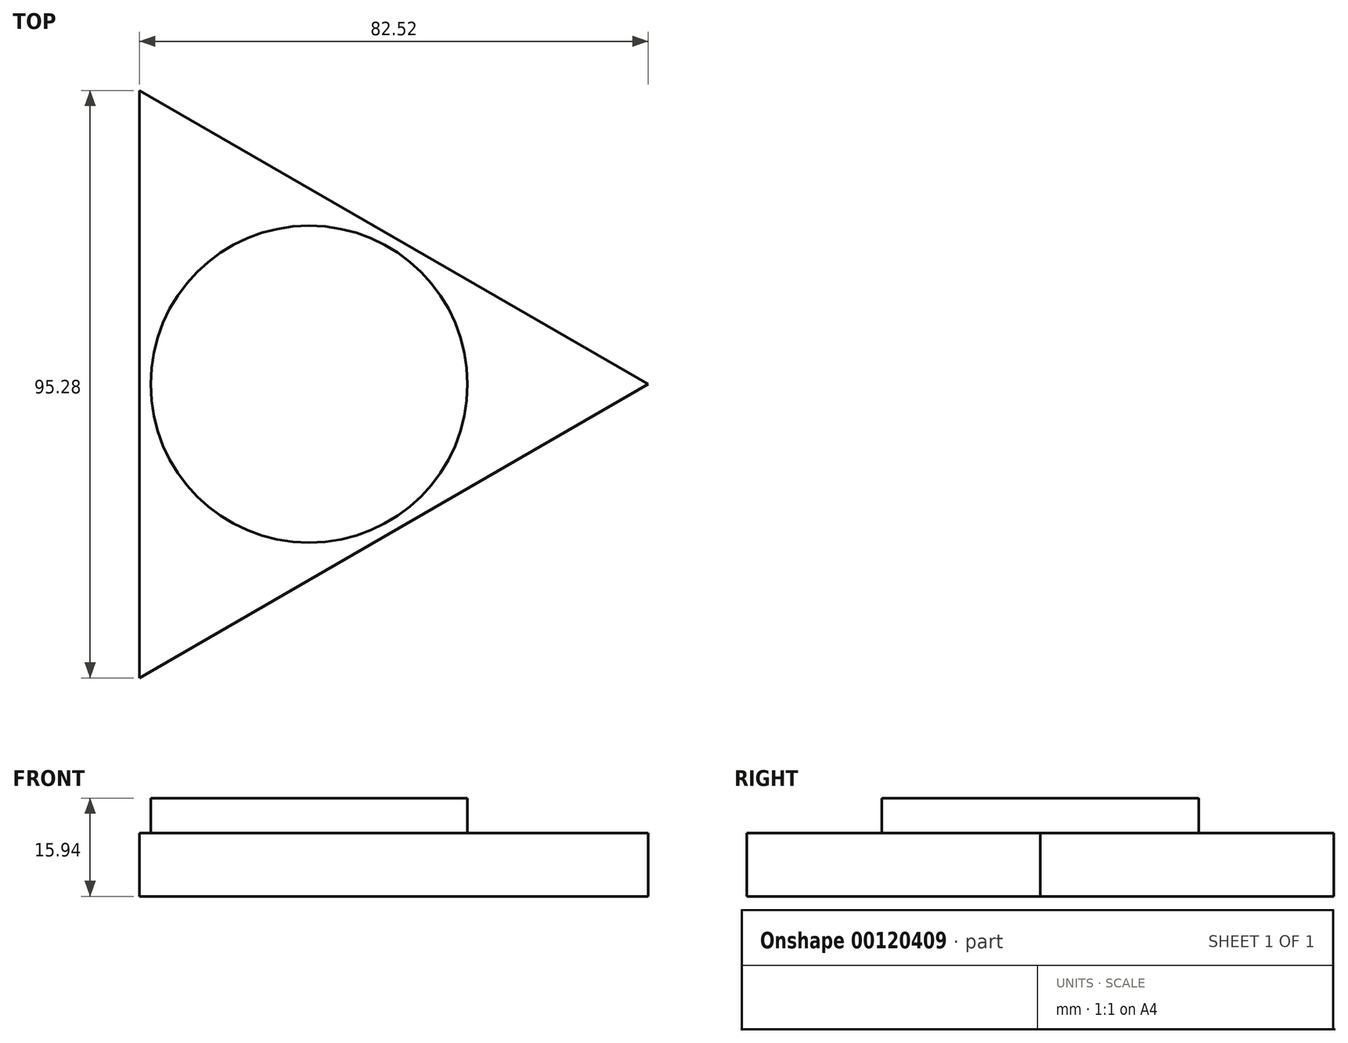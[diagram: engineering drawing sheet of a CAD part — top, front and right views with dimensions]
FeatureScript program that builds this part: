
annotation { "Feature Type Name" : "Feature", "Feature Type Description" : "" }
export const myFeature = defineFeature(function(context is Context, id is Id, definition is map)
    precondition{}
    {
        {
            var Q0;
            Q0=qCreatedBy(makeId("Top.planeOp"),FACE);
            var sketch = newSketch(context, id + "F0", { "sketchPlane" : qUnion([Q0])});
            skCircle(sketch, "E0.cCircle", {"center": v(0, 0) * mm, "radius": 27.5 * mm, "construction": true});
            skLineSegment(sketch, "E0.0", {"start": v(-27.5, -47.64) * mm, "end": v(-27.5, 47.64) * mm});
            skLineSegment(sketch, "E0.1", {"start": v(-27.5, 47.64) * mm, "end": v(55.01, 0) * mm});
            skLineSegment(sketch, "E0.2", {"start": v(55.01, 0) * mm, "end": v(-27.5, -47.64) * mm});
            skPoint(sketch, "E0.0.midPoint", {"position": v(-27.5, 0) * mm});
            skSolve(sketch);
        }
        {
            var Q0;
            Q0 = qSketchRegion(id + "F0", true);
            extrude(context, id + "F1", {"entities" : qUnion([Q0]), "depth" : 10.24 * mm});
        }
        {
            var Q0;
            Q0=makeQuery(id+"F1.opExtrude","CAP_FACE",FACE,{"disambiguationData":[OSD([sQuery(id+"F0.wireOp",EDGE,"E0.0"),sQuery(id+"F0.wireOp",EDGE,"E0.1"),sQuery(id+"F0.wireOp",EDGE,"E0.2")])],"isStart":false});
            var sketch = newSketch(context, id + "F2", { "sketchPlane" : qUnion([Q0])});
            skCircle(sketch, "E1", {"center": v(0, 0) * mm, "radius": 25.72 * mm});
            skSolve(sketch);
        }
        {
            var Q0;
            Q0 = qSketchRegion(id + "F2", true);
            extrude(context, id + "F3", {"entities" : qUnion([Q0]), "operationType" : NewBodyOperationType.ADD, "depth" : 5.7 * mm});
        }
    });
